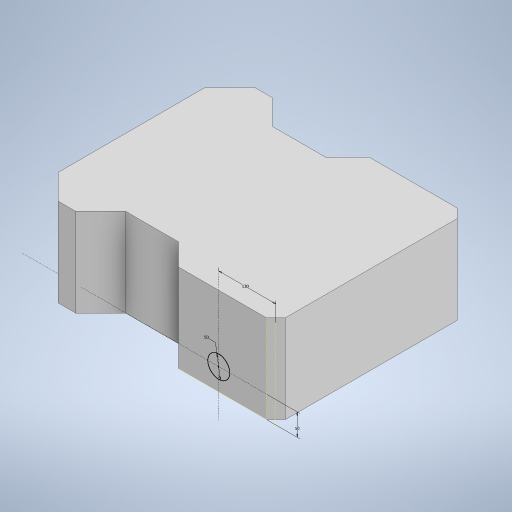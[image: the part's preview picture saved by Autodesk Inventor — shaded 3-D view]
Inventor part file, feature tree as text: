
AUTODESK INVENTOR PART (.ipt)
format: ipt  version: 2024 (Build 280153000, 153)  size: 226,304 bytes
history: native  units: mm
features: sketch x3, other x2, extrude x1
ambient origin geometry x8: Origin, YZ Plane, XZ Plane, XY Plane, X Axis, Y Axis, Z Axis, Center Point
bodies: Solid1 (feature_tree)
feature tree (6):
  other  "Frame"
  extrude  "Extrusion1"  Depth=390.0mm
  sketch  "Sketch2"  dims[d2=45.0deg]
  other  "Work Point1"
  sketch  "Sketch3"  dims[d3=70.0mm d4=135.0deg d5=200.0mm d6=120.0mm d7=80.0mm d8=135.0deg d9=226.066017mm d10=21.213203mm d11=40.0mm d12=80.0mm d15=543.847763mm d16=200.0mm d17=0.0mm d18=50.0mm d19=130.0mm d20=50.0mm]
  sketch  "Sketch1"  dims[d0=390.0mm d1=30.0mm]
